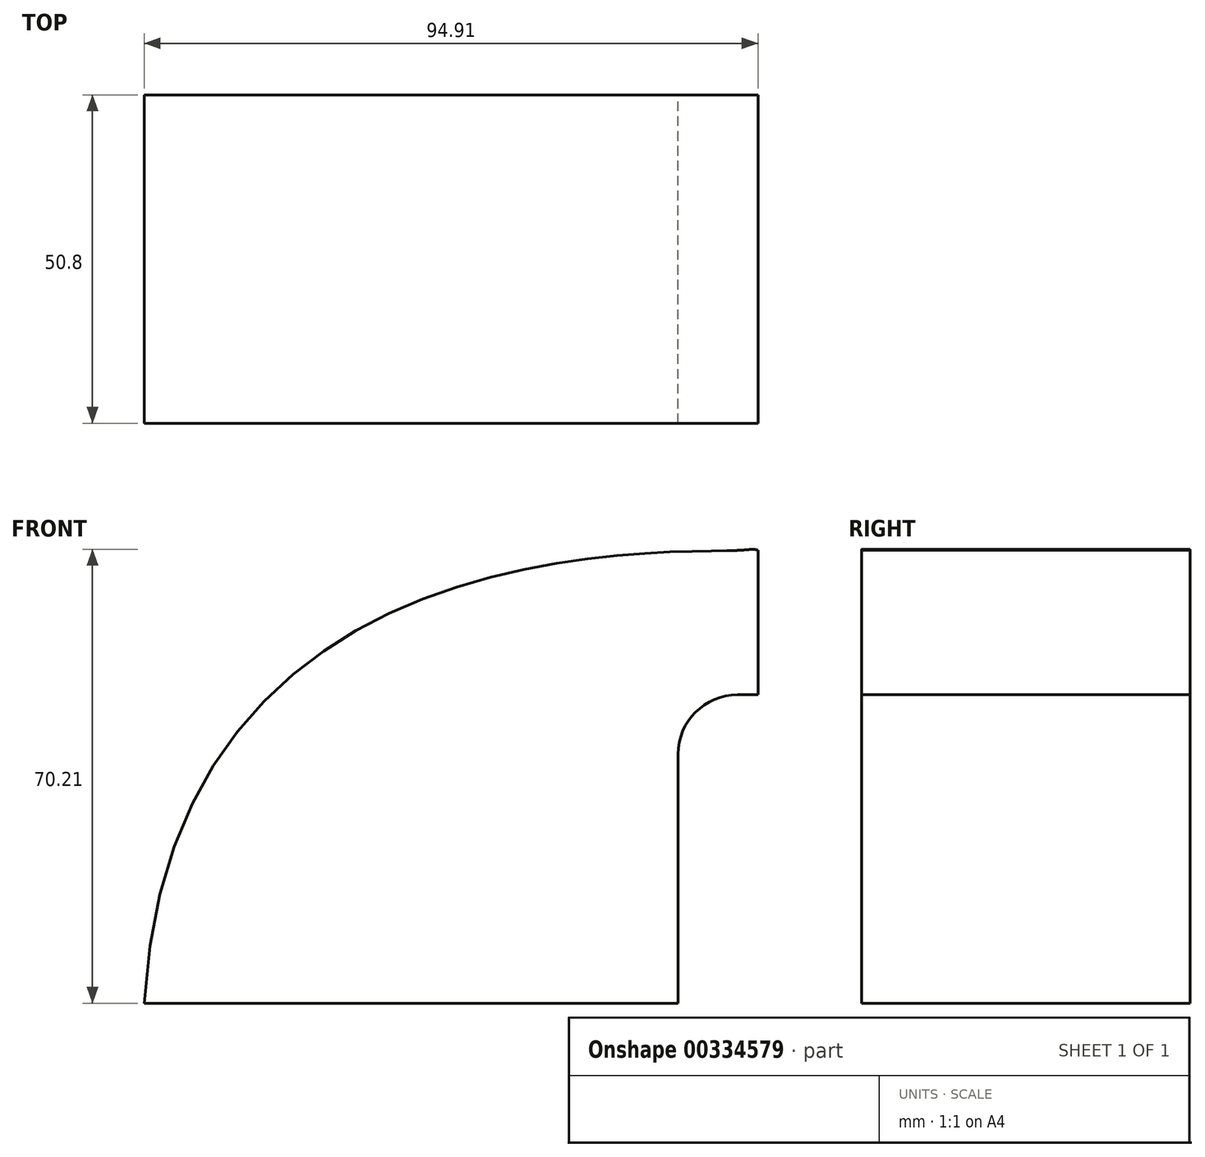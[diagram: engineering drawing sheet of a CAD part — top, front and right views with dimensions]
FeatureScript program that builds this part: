
annotation { "Feature Type Name" : "Feature", "Feature Type Description" : "" }
export const myFeature = defineFeature(function(context is Context, id is Id, definition is map)
    precondition{}
    {
        {
            var Q0;
            Q0=qCreatedBy(makeId("Front.planeOp"),FACE);
            var sketch = newSketch(context, id + "F0", { "sketchPlane" : qUnion([Q0])});
            skLineSegment(sketch, "E0.bottom", {"start": v(41.27, 9.53) * mm, "end": v(-41.28, 9.53) * mm});
            skLineSegment(sketch, "E0.top", {"start": v(41.28, -9.52) * mm, "end": v(-41.27, -9.52) * mm});
            skLineSegment(sketch, "E0.left", {"start": v(41.28, 9.53) * mm, "end": v(41.28, -9.52) * mm});
            skLineSegment(sketch, "E0.right", {"start": v(-41.28, 9.53) * mm, "end": v(-41.27, -9.52) * mm});
            skPoint(sketch, "E0.middle", {"position": v(0, 0) * mm});
            skLineSegment(sketch, "E1.bottom", {"start": v(85.38, 22.45) * mm, "end": v(53.63, 22.45) * mm});
            skLineSegment(sketch, "E1.top", {"start": v(85.38, 79.6) * mm, "end": v(53.63, 79.6) * mm});
            skLineSegment(sketch, "E1.left", {"start": v(85.38, 22.45) * mm, "end": v(85.38, 79.6) * mm});
            skLineSegment(sketch, "E1.right", {"start": v(53.63, 22.45) * mm, "end": v(53.63, 79.6) * mm});
            skPoint(sketch, "E1.middle", {"position": v(69.5, 51.02) * mm});
            skLineSegment(sketch, "E2", {"start": v(41.27, 9.53) * mm, "end": v(41.27, 48.02) * mm});
            skArc(sketch, "E3", {"start": v(41.27, 48.02) * mm, "mid": v(43.97, 54.52) * mm, "end": v(50.47, 57.22) * mm});
            skLineSegment(sketch, "E4", {"start": v(50.47, 57.22) * mm, "end": v(90.07, 57.22) * mm});
            skArc(sketch, "E5.0", {"start": v(18.92, 48.02) * mm, "mid": v(28.16, 70.33) * mm, "end": v(50.47, 79.57) * mm});
            skLineSegment(sketch, "E5.1", {"start": v(18.92, 9.53) * mm, "end": v(18.92, 48.02) * mm});
            skFitSpline(sketch, "E6", {"points": [v(-41.28, 9.52) * mm, v(50.47, 79.57) * mm, v(53.63, 79.6) * mm], "startDerivative": vector(14.23, 256.98) * mm, "endDerivative": vector(16.23, -5.6) * mm});
            skSolve(sketch);
        }
        {
            var Q0;
            {var subQ3=sQuery(id+"F0.wireOp",EDGE,"E5.1");Q0=makeQuery(id+"F0.imprint","IMPRINT",FACE,{"disambiguationData":[TD([[makeQuery(id+"F0.imprint","IMPRINT",EDGE,{"derivedFrom":subQ3}),1.0]])]});}
            var Q1;
            {var subQ1=sQuery(id+"F0.wireOp",EDGE,"E2");Q1=makeQuery(id+"F0.imprint","IMPRINT",FACE,{"disambiguationData":[TD([[makeQuery(id+"F0.imprint","IMPRINT",EDGE,{"derivedFrom":subQ1}),1.0]])]});}
            extrude(context, id + "F1", {"entities" : qUnion([Q0, Q1]), "endBound" : BoundingType.SYMMETRIC, "depth" : 50.8 * mm});
        }
    });
